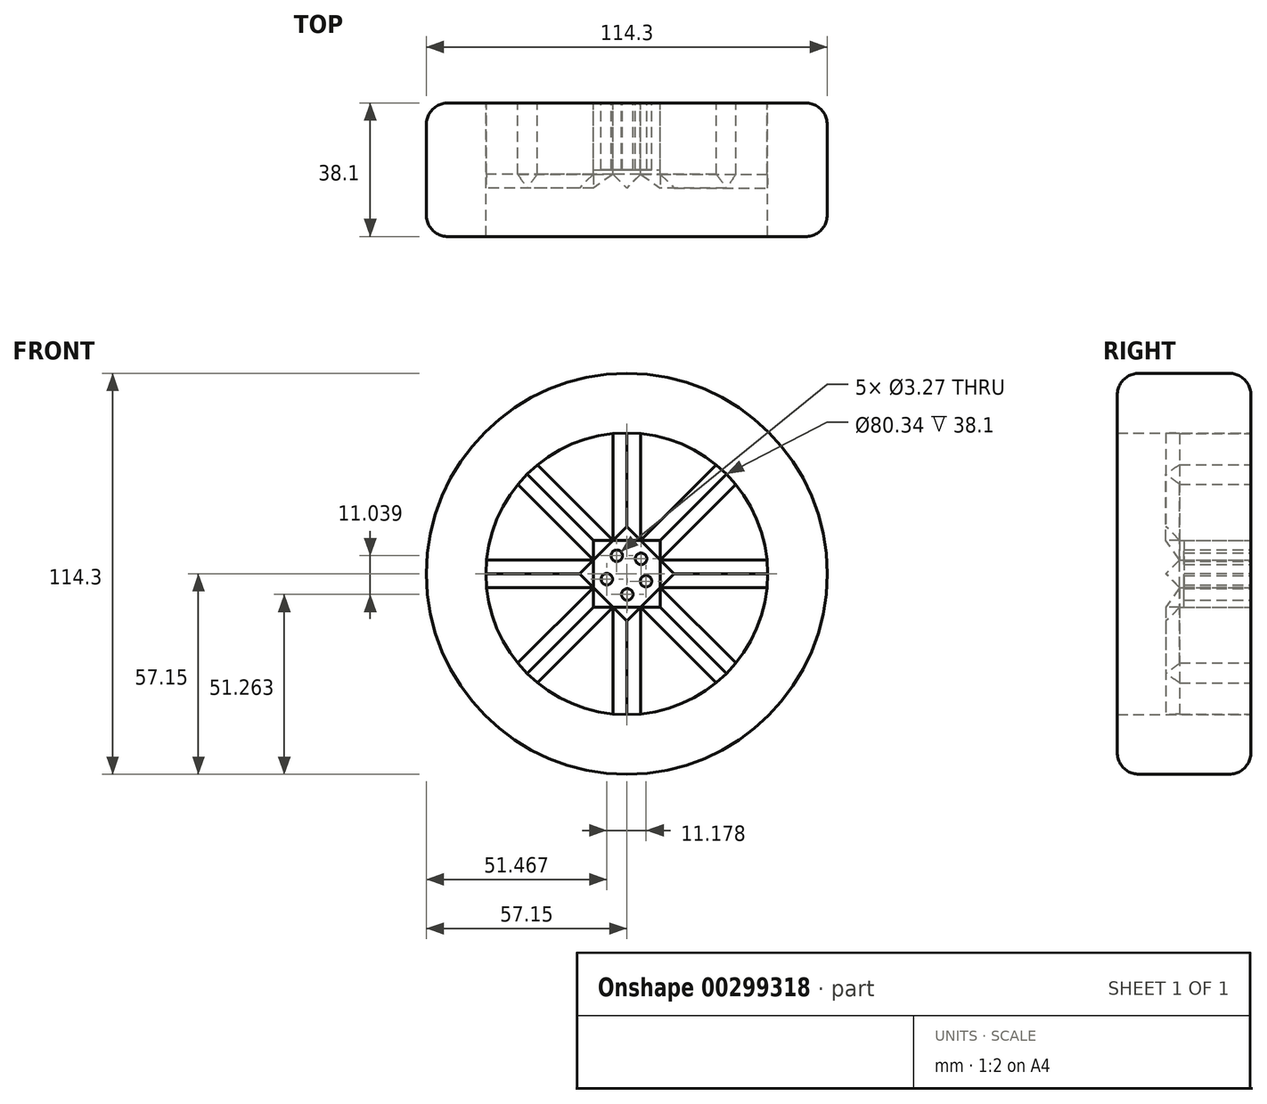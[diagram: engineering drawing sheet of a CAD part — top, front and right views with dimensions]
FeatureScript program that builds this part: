
annotation { "Feature Type Name" : "Feature", "Feature Type Description" : "" }
export const myFeature = defineFeature(function(context is Context, id is Id, definition is map)
    precondition{}
    {
        {
            var Q0;
            Q0=qCreatedBy(makeId("Front.planeOp"),FACE);
            var sketch = newSketch(context, id + "F0", { "sketchPlane" : qUnion([Q0])});
            skCircle(sketch, "E0", {"center": v(0, 0) * mm, "radius": 57.15 * mm});
            skCircle(sketch, "E1", {"center": v(0, 0) * mm, "radius": 40.17 * mm});
            skCircle(sketch, "E2.cCircle", {"center": v(0, 0) * mm, "radius": 9.54 * mm, "construction": true});
            skLineSegment(sketch, "E2.0", {"start": v(-3.95, 9.54) * mm, "end": v(3.95, 9.54) * mm});
            skLineSegment(sketch, "E2.1", {"start": v(3.95, 9.54) * mm, "end": v(9.54, 3.95) * mm});
            skLineSegment(sketch, "E2.2", {"start": v(9.54, 3.95) * mm, "end": v(9.54, -3.95) * mm});
            skLineSegment(sketch, "E2.3", {"start": v(9.54, -3.95) * mm, "end": v(3.95, -9.54) * mm});
            skLineSegment(sketch, "E2.4", {"start": v(3.95, -9.54) * mm, "end": v(-3.95, -9.54) * mm});
            skLineSegment(sketch, "E2.5", {"start": v(-3.95, -9.54) * mm, "end": v(-9.54, -3.95) * mm});
            skLineSegment(sketch, "E2.6", {"start": v(-9.54, -3.95) * mm, "end": v(-9.54, 3.95) * mm});
            skLineSegment(sketch, "E2.7", {"start": v(-9.54, 3.95) * mm, "end": v(-3.95, 9.54) * mm});
            skPoint(sketch, "E2.0.midPoint", {"position": v(0, 9.54) * mm});
            skLineSegment(sketch, "E3", {"start": v(-3.95, 9.54) * mm, "end": v(-3.95, 39.98) * mm});
            skPoint(sketch, "E4.endSnap0", {"position": v(6.75, 6.75) * mm});
            skLineSegment(sketch, "E5", {"start": v(3.95, 9.54) * mm, "end": v(3.95, 39.98) * mm});
            skLineSegment(sketch, "E6", {"start": v(3.95, 9.54) * mm, "end": v(25.47, 31.06) * mm});
            skLineSegment(sketch, "E7", {"start": v(9.54, 3.95) * mm, "end": v(31.06, 25.47) * mm});
            skLineSegment(sketch, "E8", {"start": v(9.54, 3.95) * mm, "end": v(39.98, 3.95) * mm});
            skLineSegment(sketch, "E9", {"start": v(9.54, -3.95) * mm, "end": v(39.98, -3.95) * mm});
            skLineSegment(sketch, "E10", {"start": v(9.54, -3.95) * mm, "end": v(31.06, -25.47) * mm});
            skLineSegment(sketch, "E11", {"start": v(3.95, -9.54) * mm, "end": v(25.47, -31.06) * mm});
            skLineSegment(sketch, "E12", {"start": v(3.95, -9.54) * mm, "end": v(3.95, -39.98) * mm});
            skLineSegment(sketch, "E13", {"start": v(-3.95, -9.54) * mm, "end": v(-3.95, -39.98) * mm});
            skLineSegment(sketch, "E14", {"start": v(-9.54, -3.95) * mm, "end": v(-31.06, -25.47) * mm});
            skLineSegment(sketch, "E15", {"start": v(-3.95, -9.54) * mm, "end": v(-25.47, -31.06) * mm});
            skLineSegment(sketch, "E16", {"start": v(-9.54, -3.95) * mm, "end": v(-39.98, -3.95) * mm});
            skLineSegment(sketch, "E17", {"start": v(-9.54, 3.95) * mm, "end": v(-39.98, 3.95) * mm});
            skLineSegment(sketch, "E18", {"start": v(-9.54, 3.95) * mm, "end": v(-31.06, 25.47) * mm});
            skLineSegment(sketch, "E19", {"start": v(-3.95, 9.54) * mm, "end": v(-25.47, 31.06) * mm});
            skCircle(sketch, "E20", {"center": v(4.06, 4.26) * mm, "radius": 1.64 * mm});
            skCircle(sketch, "E21.1.0", {"center": v(5.5, -2.12) * mm, "radius": 1.64 * mm});
            skCircle(sketch, "E21.2.0", {"center": v(0.14, -5.89) * mm, "radius": 1.64 * mm});
            skLineSegment(sketch, "E21.anchor1", {"start": v(0, 0) * mm, "end": v(4.06, 4.26) * mm, "construction": true});
            skLineSegment(sketch, "E21.anchor2", {"start": v(0, 0) * mm, "end": v(0.14, -5.89) * mm, "construction": true});
            skCircle(sketch, "E22.1.0", {"center": v(-5.68, -1.54) * mm, "radius": 1.64 * mm});
            skCircle(sketch, "E22.2.0", {"center": v(-2.85, 5.15) * mm, "radius": 1.64 * mm});
            skLineSegment(sketch, "E22.anchor2", {"start": v(0, 0) * mm, "end": v(-2.85, 5.15) * mm, "construction": true});
            skSolve(sketch);
        }
        {
            var Q0;
            Q0=makeQuery(id+"F0.imprint","IMPRINT",FACE,{"disambiguationData":[TD([[makeQuery(id+"F0.imprint","IMPRINT",EDGE,{"derivedFrom":sQuery(id+"F0.wireOp",EDGE,"E0")}),1.0]])]});
            extrude(context, id + "F1", {"entities" : qUnion([Q0]), "depth" : 38.1 * mm});
        }
        {
            var Q0;
            Q0=makeQuery(id+"F0.imprint","IMPRINT",FACE,{"disambiguationData":[TD([[makeQuery(id+"F0.imprint","IMPRINT",EDGE,{"derivedFrom":sQuery(id+"F0.wireOp",EDGE,"E2.6")}),1.0]])]});
            var Q1;
            Q1=makeQuery(id+"F0.imprint","IMPRINT",FACE,{"disambiguationData":[TD([[makeQuery(id+"F0.imprint","IMPRINT",EDGE,{"derivedFrom":sQuery(id+"F0.wireOp",EDGE,"E2.7")}),1.0]])]});
            var Q2;
            Q2=makeQuery(id+"F0.imprint","IMPRINT",FACE,{"disambiguationData":[TD([[makeQuery(id+"F0.imprint","IMPRINT",EDGE,{"derivedFrom":sQuery(id+"F0.wireOp",EDGE,"E2.1")}),1.0]])]});
            var Q3;
            Q3=makeQuery(id+"F0.imprint","IMPRINT",FACE,{"disambiguationData":[TD([[makeQuery(id+"F0.imprint","IMPRINT",EDGE,{"derivedFrom":sQuery(id+"F0.wireOp",EDGE,"E2.0")}),1.0]])]});
            var Q4;
            Q4=makeQuery(id+"F0.imprint","IMPRINT",FACE,{"disambiguationData":[TD([[makeQuery(id+"F0.imprint","IMPRINT",EDGE,{"derivedFrom":sQuery(id+"F0.wireOp",EDGE,"E2.2")}),1.0]])]});
            var Q5;
            Q5=makeQuery(id+"F0.imprint","IMPRINT",FACE,{"disambiguationData":[TD([[makeQuery(id+"F0.imprint","IMPRINT",EDGE,{"derivedFrom":sQuery(id+"F0.wireOp",EDGE,"E2.3")}),1.0]])]});
            var Q6;
            Q6=makeQuery(id+"F0.imprint","IMPRINT",FACE,{"disambiguationData":[TD([[makeQuery(id+"F0.imprint","IMPRINT",EDGE,{"derivedFrom":sQuery(id+"F0.wireOp",EDGE,"E2.4")}),1.0]])]});
            var Q7;
            Q7=makeQuery(id+"F0.imprint","IMPRINT",FACE,{"disambiguationData":[TD([[makeQuery(id+"F0.imprint","IMPRINT",EDGE,{"derivedFrom":sQuery(id+"F0.wireOp",EDGE,"E2.5")}),1.0]])]});
            extrude(context, id + "F2", {"entities" : qUnion([Q0, Q1, Q2, Q3, Q4, Q5, Q6, Q7]), "depth" : 25.4 * mm});
        }
        {
            var Q0;
            Q0=makeQuery(id+"F0.imprint","IMPRINT",FACE,{"disambiguationData":[TD([[makeQuery(id+"F0.imprint","IMPRINT",EDGE,{"derivedFrom":sQuery(id+"F0.wireOp",EDGE,"E2.0")}),-1.0]])]});
            extrude(context, id + "F3", {"entities" : qUnion([Q0]), "depth" : 19.05 * mm});
        }
        {
            var Q0;
            Q0=makeQuery(id+"F1.opExtrude","CAP_EDGE",EDGE,{"disambiguationData":[OSD([sQuery(id+"F0.wireOp",EDGE,"E0")])],"isStart":false});
            var Q1;
            Q1=makeQuery(id+"F1.opExtrude","CAP_EDGE",EDGE,{"disambiguationData":[OSD([sQuery(id+"F0.wireOp",EDGE,"E0")])],"isStart":true});
            fillet(context, id + "F4", {"entities" : qUnion([Q0, Q1]), "radius" : 6.13 * mm, "tangentPropagation" : true, "allowEdgeOverflow" : false});
        }
        {
            var Q0;
            Q0=makeQuery(id+"F2.opExtrude","CAP_EDGE",EDGE,{"disambiguationData":[OSD([sQuery(id+"F0.wireOp",EDGE,"E2.1")])],"isStart":false});
            var Q1;
            Q1=makeQuery(id+"F2.opExtrude","CAP_EDGE",EDGE,{"disambiguationData":[OSD([sQuery(id+"F0.wireOp",EDGE,"E2.0")])],"isStart":false});
            var Q2;
            Q2=makeQuery(id+"F2.opExtrude","CAP_EDGE",EDGE,{"disambiguationData":[OSD([sQuery(id+"F0.wireOp",EDGE,"E2.7")])],"isStart":false});
            var Q3;
            Q3=makeQuery(id+"F2.opExtrude","CAP_EDGE",EDGE,{"disambiguationData":[OSD([sQuery(id+"F0.wireOp",EDGE,"E2.6")])],"isStart":false});
            var Q4;
            Q4=makeQuery(id+"F2.opExtrude","CAP_EDGE",EDGE,{"disambiguationData":[OSD([sQuery(id+"F0.wireOp",EDGE,"E2.5")])],"isStart":false});
            var Q5;
            Q5=makeQuery(id+"F2.opExtrude","CAP_EDGE",EDGE,{"disambiguationData":[OSD([sQuery(id+"F0.wireOp",EDGE,"E2.4")])],"isStart":false});
            var Q6;
            Q6=makeQuery(id+"F2.opExtrude","CAP_EDGE",EDGE,{"disambiguationData":[OSD([sQuery(id+"F0.wireOp",EDGE,"E2.3")])],"isStart":false});
            var Q7;
            Q7=makeQuery(id+"F2.opExtrude","CAP_EDGE",EDGE,{"disambiguationData":[OSD([sQuery(id+"F0.wireOp",EDGE,"E2.2")])],"isStart":false});
            chamfer(context, id + "F5", {"entities" : qUnion([Q0, Q1, Q2, Q3, Q4, Q5, Q6, Q7]), "width" : 5.08 * mm, "tangentPropagation" : true});
        }
        {
            var Q0;
            Q0=makeQuery(id+"F2.opExtrude","CAP_EDGE",EDGE,{"disambiguationData":[OSD([sQuery(id+"F0.wireOp",EDGE,"E3")])],"isStart":false});
            var Q1;
            Q1=makeQuery(id+"F2.opExtrude","CAP_EDGE",EDGE,{"disambiguationData":[OSD([sQuery(id+"F0.wireOp",EDGE,"E5")])],"isStart":false});
            var Q2;
            Q2=makeQuery(id+"F2.opExtrude","CAP_EDGE",EDGE,{"disambiguationData":[OSD([sQuery(id+"F0.wireOp",EDGE,"E19")])],"isStart":false});
            var Q3;
            Q3=makeQuery(id+"F2.opExtrude","CAP_EDGE",EDGE,{"disambiguationData":[OSD([sQuery(id+"F0.wireOp",EDGE,"E18")])],"isStart":false});
            var Q4;
            Q4=makeQuery(id+"F2.opExtrude","CAP_EDGE",EDGE,{"disambiguationData":[OSD([sQuery(id+"F0.wireOp",EDGE,"E17")])],"isStart":false});
            var Q5;
            Q5=makeQuery(id+"F2.opExtrude","CAP_EDGE",EDGE,{"disambiguationData":[OSD([sQuery(id+"F0.wireOp",EDGE,"E16")])],"isStart":false});
            var Q6;
            Q6=makeQuery(id+"F2.opExtrude","CAP_EDGE",EDGE,{"disambiguationData":[OSD([sQuery(id+"F0.wireOp",EDGE,"E14")])],"isStart":false});
            var Q7;
            Q7=makeQuery(id+"F2.opExtrude","CAP_EDGE",EDGE,{"disambiguationData":[OSD([sQuery(id+"F0.wireOp",EDGE,"E15")])],"isStart":false});
            var Q8;
            Q8=makeQuery(id+"F2.opExtrude","CAP_EDGE",EDGE,{"disambiguationData":[OSD([sQuery(id+"F0.wireOp",EDGE,"E13")])],"isStart":false});
            var Q9;
            Q9=makeQuery(id+"F2.opExtrude","CAP_EDGE",EDGE,{"disambiguationData":[OSD([sQuery(id+"F0.wireOp",EDGE,"E12")])],"isStart":false});
            var Q10;
            Q10=makeQuery(id+"F2.opExtrude","CAP_EDGE",EDGE,{"disambiguationData":[OSD([sQuery(id+"F0.wireOp",EDGE,"E11")])],"isStart":false});
            var Q11;
            Q11=makeQuery(id+"F2.opExtrude","CAP_EDGE",EDGE,{"disambiguationData":[OSD([sQuery(id+"F0.wireOp",EDGE,"E10")])],"isStart":false});
            var Q12;
            Q12=makeQuery(id+"F2.opExtrude","CAP_EDGE",EDGE,{"disambiguationData":[OSD([sQuery(id+"F0.wireOp",EDGE,"E9")])],"isStart":false});
            var Q13;
            Q13=makeQuery(id+"F2.opExtrude","CAP_EDGE",EDGE,{"disambiguationData":[OSD([sQuery(id+"F0.wireOp",EDGE,"E8")])],"isStart":false});
            var Q14;
            Q14=makeQuery(id+"F2.opExtrude","CAP_EDGE",EDGE,{"disambiguationData":[OSD([sQuery(id+"F0.wireOp",EDGE,"E7")])],"isStart":false});
            var Q15;
            Q15=makeQuery(id+"F2.opExtrude","CAP_EDGE",EDGE,{"disambiguationData":[OSD([sQuery(id+"F0.wireOp",EDGE,"E6")])],"isStart":false});
            chamfer(context, id + "F6", {"entities" : qUnion([Q0, Q1, Q2, Q3, Q4, Q5, Q6, Q7, Q8, Q9, Q10, Q11, Q12, Q13, Q14, Q15]), "width" : 5.08 * mm, "tangentPropagation" : true});
        }
    });
